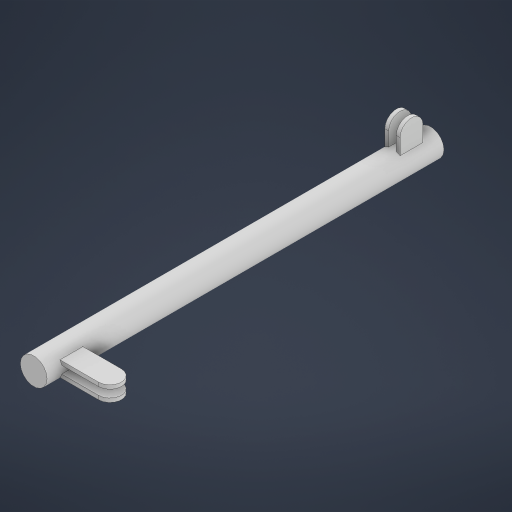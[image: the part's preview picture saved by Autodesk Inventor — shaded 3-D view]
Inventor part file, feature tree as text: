
AUTODESK INVENTOR PART (.ipt)
format: ipt  version: 2023 (Build 270158000, 158)  size: 225,280 bytes
history: native  units: in
note: dims shown in document units (in); Inventor stores cm internally (conversion verified against a paired STEP export)
features: extrude x3, sketch x3, fillet x1
ambient origin geometry x8: Origin, YZ Plane, XZ Plane, XY Plane, X Axis, Y Axis, Z Axis, Center Point
bodies: Solid1 (feature_tree)
feature tree (7):
  extrude  "Extrusion1"  Depth=52.0in TaperAngle=0.0deg
  extrude  "Extrusion2"  Depth=0.5in
  extrude  "Extrusion3"  Depth=2.0in
  fillet  "Fillet1"  Radius=5.0in
  sketch  "Sketch1"  dims[d0=3.5in d1=52.0in d2=0.0in]
  sketch  "Sketch2"  dims[d3=3.0in d4=0.5in]
  sketch  "Sketch3"  dims[d5=0.5in d6=2.0in d7=5.0in d8=0.0in d9=1.5in d10=0.5in d11=0.5in d12=3.0in d13=2.0in d14=8.0in d15=0.0in]
